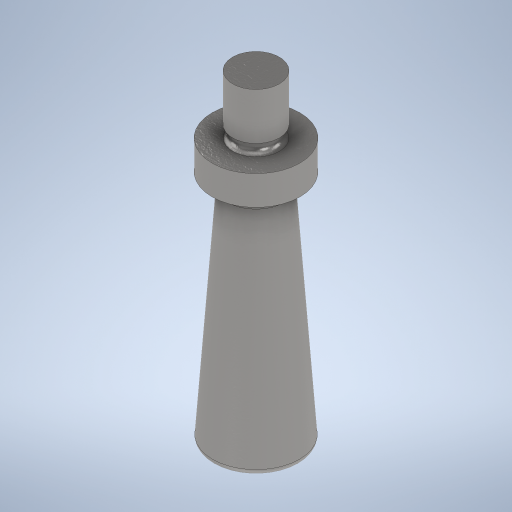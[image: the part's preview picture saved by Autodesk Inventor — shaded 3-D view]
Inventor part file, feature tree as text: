
AUTODESK INVENTOR PART (.ipt)
format: ipt  version: 2024 (Build 280153000, 153)  size: 300,544 bytes
history: native  units: mm
features: fillet x2, revolve x1, sketch x1
ambient origin geometry x8: Origin, YZ Plane, XZ Plane, XY Plane, X Axis, Y Axis, Z Axis, Center Point
bodies: Volumenkörper1 (feature_tree)
feature tree (4):
  revolve  "Umdrehung1"
  fillet  "Rundung1"  Radius=0.698132mm
  fillet  "Rundung2"  Radius=5.0mm
  sketch  "Skizze1"  dims[d2=8.0mm d3=15.0mm d4=8.0mm d5=10.0mm d6=55.0mm d7=15.0mm d8=90.0deg d9=2.0mm d10=1.0mm]
